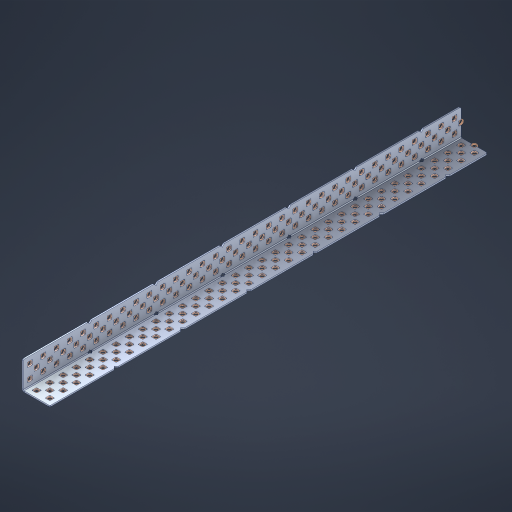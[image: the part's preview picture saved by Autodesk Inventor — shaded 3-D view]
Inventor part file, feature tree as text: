
AUTODESK INVENTOR PART (.ipt)
format: ipt  version: 2023 (Build 270158000, 158)  size: 2,227,200 bytes
history: native  units: in
note: dims shown in document units (in); Inventor stores cm internally (conversion verified against a paired STEP export)
features: other x204, extrude x196, sheet_metal_op x8, sketch x7, pattern_linear x2, mirror x1, chamfer x1
ambient origin geometry x8: Origin, YZ Plane, XZ Plane, XY Plane, X Axis, Y Axis, Z Axis, Center Point
bodies: Solid1 (feature_tree), Body (feature_tree)
feature tree (419):
  sheet_metal_op  "Flanges"
  sheet_metal_op  "Body Pattern"
  pattern_linear  "Center Pattern"  Spacing1=1.0in  [1 undecoded]
  other  "Arc Length"
  pattern_linear  "Notch Pattern"  Spacing1=0.1875in  [1 undecoded]
  other  "Diagonal Plane"
  mirror  "Everything Mirrored"
  chamfer  "End Chamfer"
  sketch  "Sketch1"  dims[d0=1.0in]
  other  "Plate1"
  sketch  "Sketch2"  dims[d1=16.5in]
  other  "Plate2"
  sheet_metal_op  "Bend1"
  sheet_metal_op  "Corner1"
  sketch  "Sketch8"  dims[d2=0.0469in]
  sketch  "Sketch9"  dims[d3=0.0469in]
  other  "Srf91"
  sheet_metal_op  "Body Pattern Sketch"
  other  "Srf92"
  sketch  "Sketch13"  dims[d4=0.0234in]
  sketch  "Sketch15"  dims[d5=0.0938in]
  sketch  "Sketch16"  dims[d6=0.0469in d7=1.0in d8=90.0deg d9=0.0312in d10=0.1875in d11=0.0469in d12=0.0469in d49=0.182in d50=0.02in d52=0.25in d53=0.0469in d54=0.0in d55=0.172in d56=1.0in d57=0.0in d60=12.9921in d62=0.5in d63=0.7874in d65=0.5in d85=0.1473in d86=0.1659in d89=0.0469in d90=0.0in d91=0.04in d92=0.0491in d95=2.5in d96=0.04in d97=0.25in d98=45.0deg d99=0.25in d106=0.182in d107=0.02in d108=0.5in d110=0.0469in d111=0.0in d112=0.172in d113=0.5in d114=0.0in d117=0.5in d123=0.25in d125=0.25in d126=0.0491in d127=0.1227in d128=0.08in d129=0.04in d130=2.5in]
  other  "Srf786"
  other  "Srf856"
  other  "Srf857"
  other  "Srf858"
  other  "Srf859"
  other  "Srf860"
  other  "Srf861"
  other  "Srf889"
  other  "Srf890"
  other  "Srf891"
  other  "Srf1275"
  other  "Srf1276"
  other  "Srf1278"
  other  "Srf1279"
  other  "Srf1280"
  other  "Srf1281"
  other  "Srf1282"
  other  "Srf1283"
  other  "Srf1277"
  other  "Srf1285"
  other  "Srf1286"
  other  "Srf1287"
  other  "Srf1383"
  other  "Srf1384"
  other  "Srf1385"
  other  "Srf1386"
  other  "Srf1387"
  other  "Srf1388"
  other  "Srf1389"
  other  "Srf1390"
  other  "Srf1391"
  other  "Srf1392"
  other  "Srf1393"
  other  "Srf1394"
  other  "Srf1395"
  other  "Srf1396"
  other  "Srf1397"
  other  "Srf1398"
  other  "Srf1399"
  other  "Srf1400"
  other  "Srf1401"
  other  "Srf1402"
  other  "Srf1403"
  other  "Srf1404"
  other  "Srf1405"
  other  "Srf1406"
  other  "Srf1407"
  other  "Srf1408"
  other  "Srf1409"
  other  "Srf1410"
  other  "Srf1411"
  other  "Srf1412"
  other  "Srf1413"
  other  "Srf1414"
  other  "Srf1415"
  other  "Srf1416"
  other  "Srf1417"
  other  "Srf1418"
  other  "Srf1419"
  other  "Srf1420"
  other  "Srf1421"
  other  "Srf1422"
  other  "Srf1423"
  other  "Srf1424"
  other  "Srf1425"
  other  "Srf1426"
  other  "Srf1427"
  other  "Srf1428"
  other  "Srf1429"
  other  "Srf1430"
  other  "Srf1431"
  other  "Srf1432"
  other  "Srf1433"
  other  "Srf1434"
  other  "Srf1435"
  other  "Srf1436"
  other  "Srf1437"
  other  "Srf1438"
  other  "Srf1439"
  other  "Srf1440"
  other  "Srf1445"
  other  "Srf1446"
  other  "Srf1447"
  other  "Srf1448"
  other  "Srf1449"
  other  "Srf1450"
  other  "Srf1451"
  other  "Srf1452"
  other  "Srf1453"
  other  "Srf1454"
  other  "Srf1455"
  other  "Srf1456"
  other  "Srf1457"
  other  "Srf1458"
  other  "Srf1459"
  other  "Srf1460"
  other  "Srf1461"
  other  "Srf1462"
  other  "Srf1463"
  other  "Srf1464"
  other  "Srf1465"
  other  "Srf1466"
  other  "Srf1467"
  other  "Srf1468"
  other  "Srf1469"
  other  "Srf1470"
  other  "Srf1471"
  other  "Srf1472"
  other  "Srf1473"
  other  "Srf1475"
  other  "Srf1476"
  other  "Srf1477"
  other  "Srf1478"
  other  "Srf1479"
  other  "Srf1480"
  other  "Srf1481"
  other  "Srf1482"
  other  "Srf1483"
  other  "Srf1484"
  other  "Srf1485"
  other  "Srf1486"
  other  "Srf1487"
  other  "Srf1488"
  other  "Srf1489"
  other  "Srf1490"
  other  "Srf1491"
  other  "Srf1492"
  other  "Srf1493"
  other  "Srf1494"
  other  "Srf1495"
  other  "Srf1496"
  other  "Srf1497"
  other  "Srf1498"
  other  "Srf1499"
  other  "Srf1500"
  other  "Srf1501"
  other  "Srf1502"
  other  "Srf1503"
  other  "Srf1504"
  other  "Srf1505"
  other  "Srf1506"
  other  "Srf1507"
  other  "Srf1508"
  other  "Srf1509"
  other  "Srf1510"
  other  "Srf1511"
  other  "Srf1512"
  other  "Srf1513"
  other  "Srf1514"
  other  "Srf1515"
  other  "Srf1516"
  other  "Srf1517"
  other  "Srf1518"
  other  "Srf1519"
  other  "Srf1520"
  other  "Srf1521"
  other  "Srf1522"
  other  "Srf1523"
  other  "Srf1524"
  other  "Srf1525"
  other  "Srf1526"
  other  "Srf1527"
  other  "Srf1528"
  other  "Srf1529"
  other  "Srf1530"
  other  "Srf1531"
  other  "Srf1532"
  other  "Srf1537"
  other  "Srf1538"
  other  "Srf1539"
  other  "Srf1540"
  other  "Srf1541"
  other  "Srf1542"
  other  "Srf1543"
  other  "Srf1544"
  other  "Srf1545"
  other  "Srf1546"
  other  "Srf1547"
  other  "Srf1548"
  other  "Srf1549"
  other  "Srf1550"
  other  "Srf1551"
  other  "Srf1552"
  other  "Srf1553"
  other  "Srf1554"
  other  "Srf1555"
  other  "Srf1556"
  other  "Srf1557"
  other  "Srf1558"
  other  "Srf1559"
  other  "Srf1560"
  other  "Srf1561"
  other  "Srf1562"
  other  "Srf1563"
  other  "Srf1564"
  other  "Srf1565"
  sheet_metal_op  "Body Stamp"
  sheet_metal_op  "Body Circle"
  other  "Center Stamp"
  other  "Center Circle"
  sheet_metal_op  "Notch"
  extrude  "ExtrusionSrf92"  Depth=0.0469in
  extrude  "ExtrusionSrf856"  Depth=0.0469in
  extrude  "ExtrusionSrf857"  Depth=0.182in
  extrude  "ExtrusionSrf858"  Depth=0.02in
  extrude  "ExtrusionSrf859"  Depth=0.25in
  extrude  "ExtrusionSrf860"  Depth=0.0469in
  extrude  "ExtrusionSrf861"  TaperAngle=0.0deg  [1 undecoded]
  extrude  "ExtrusionSrf889"  Depth=2.5in
  extrude  "ExtrusionSrf890"  Depth=1.0in TaperAngle=0.0deg
  extrude  "ExtrusionSrf891"  Depth=2.5in
  extrude  "ExtrusionSrf1275"  Depth=0.5in
  extrude  "ExtrusionSrf1276"  Depth=2.5in
  extrude  "ExtrusionSrf1277"  Depth=2.5in
  extrude  "ExtrusionSrf1278"  Depth=0.0469in
  extrude  "ExtrusionSrf1279"  Depth=2.5in TaperAngle=0.0deg
  extrude  "ExtrusionSrf1280"  Depth=2.5in
  extrude  "ExtrusionSrf1281"  Depth=0.25in TaperAngle=45.0deg
  extrude  "ExtrusionSrf1282"  Depth=0.25in
  extrude  "ExtrusionSrf1345"  Depth=0.182in
  extrude  "ExtrusionSrf1346"  Depth=0.02in
  extrude  "ExtrusionSrf1347"  Depth=0.5in
  extrude  "ExtrusionSrf1348"  Depth=0.0469in
  extrude  "ExtrusionSrf1383"  TaperAngle=0.0deg  [1 undecoded]
  extrude  "ExtrusionSrf1384"  Depth=2.5in
  extrude  "ExtrusionSrf1385"  Depth=0.5in TaperAngle=0.0deg
  extrude  "ExtrusionSrf1386"  Depth=0.5in
  extrude  "ExtrusionSrf1387"  Depth=0.25in
  extrude  "ExtrusionSrf1388"  Depth=0.25in
  extrude  "ExtrusionSrf1389"  Depth=2.5in
  extrude  "ExtrusionSrf1390"  Depth=2.5in
  extrude  "ExtrusionSrf1391"  Depth=2.5in
  extrude  "ExtrusionSrf1392"  Depth=2.5in
  extrude  "ExtrusionSrf1393"  Depth=2.5in
  extrude  "ExtrusionSrf1394"  [1 undecoded]
  extrude  "ExtrusionSrf1395"  [1 undecoded]
  extrude  "ExtrusionSrf1396"  [1 undecoded]
  extrude  "ExtrusionSrf1397"  [1 undecoded]
  extrude  "ExtrusionSrf1398"  [1 undecoded]
  extrude  "ExtrusionSrf1399"  [1 undecoded]
  extrude  "ExtrusionSrf1400"  [1 undecoded]
  extrude  "ExtrusionSrf1401"  [1 undecoded]
  extrude  "ExtrusionSrf1402"  [1 undecoded]
  extrude  "ExtrusionSrf1403"  [1 undecoded]
  extrude  "ExtrusionSrf1404"  [1 undecoded]
  extrude  "ExtrusionSrf1405"  [1 undecoded]
  extrude  "ExtrusionSrf1406"  [1 undecoded]
  extrude  "ExtrusionSrf1407"  [1 undecoded]
  extrude  "ExtrusionSrf1408"  [1 undecoded]
  extrude  "ExtrusionSrf1409"  [1 undecoded]
  extrude  "ExtrusionSrf1410"  [1 undecoded]
  extrude  "ExtrusionSrf1411"  [1 undecoded]
  extrude  "ExtrusionSrf1412"  [1 undecoded]
  extrude  "ExtrusionSrf1413"  [1 undecoded]
  extrude  "ExtrusionSrf1414"  [1 undecoded]
  extrude  "ExtrusionSrf1415"  [1 undecoded]
  extrude  "ExtrusionSrf1416"  [1 undecoded]
  extrude  "ExtrusionSrf1417"  [1 undecoded]
  extrude  "ExtrusionSrf1418"  [1 undecoded]
  extrude  "ExtrusionSrf1419"  [1 undecoded]
  extrude  "ExtrusionSrf1420"  [1 undecoded]
  extrude  "ExtrusionSrf1421"  [1 undecoded]
  extrude  "ExtrusionSrf1422"  [1 undecoded]
  extrude  "ExtrusionSrf1423"  [1 undecoded]
  extrude  "ExtrusionSrf1424"  [1 undecoded]
  extrude  "ExtrusionSrf1425"  [1 undecoded]
  extrude  "ExtrusionSrf1426"  [1 undecoded]
  extrude  "ExtrusionSrf1427"  [1 undecoded]
  extrude  "ExtrusionSrf1428"  [1 undecoded]
  extrude  "ExtrusionSrf1429"  [1 undecoded]
  extrude  "ExtrusionSrf1430"  [1 undecoded]
  extrude  "ExtrusionSrf1431"  [1 undecoded]
  extrude  "ExtrusionSrf1432"  [1 undecoded]
  extrude  "ExtrusionSrf1433"  [1 undecoded]
  extrude  "ExtrusionSrf1434"  [1 undecoded]
  extrude  "ExtrusionSrf1435"  [1 undecoded]
  extrude  "ExtrusionSrf1436"  [1 undecoded]
  extrude  "ExtrusionSrf1437"  [1 undecoded]
  extrude  "ExtrusionSrf1438"  [1 undecoded]
  extrude  "ExtrusionSrf1439"  [1 undecoded]
  extrude  "ExtrusionSrf1440"  [1 undecoded]
  extrude  "ExtrusionSrf1445"  [1 undecoded]
  extrude  "ExtrusionSrf1446"  [1 undecoded]
  extrude  "ExtrusionSrf1447"  [1 undecoded]
  extrude  "ExtrusionSrf1448"  [1 undecoded]
  extrude  "ExtrusionSrf1449"  [1 undecoded]
  extrude  "ExtrusionSrf1450"  [1 undecoded]
  extrude  "ExtrusionSrf1451"  [1 undecoded]
  extrude  "ExtrusionSrf1452"  [1 undecoded]
  extrude  "ExtrusionSrf1453"  [1 undecoded]
  extrude  "ExtrusionSrf1454"  [1 undecoded]
  extrude  "ExtrusionSrf1455"  [1 undecoded]
  extrude  "ExtrusionSrf1456"  [1 undecoded]
  extrude  "ExtrusionSrf1457"  [1 undecoded]
  extrude  "ExtrusionSrf1458"  [1 undecoded]
  extrude  "ExtrusionSrf1459"  [1 undecoded]
  extrude  "ExtrusionSrf1460"  [1 undecoded]
  extrude  "ExtrusionSrf1461"  [1 undecoded]
  extrude  "ExtrusionSrf1462"  [1 undecoded]
  extrude  "ExtrusionSrf1463"  [1 undecoded]
  extrude  "ExtrusionSrf1464"  [1 undecoded]
  extrude  "ExtrusionSrf1465"  [1 undecoded]
  extrude  "ExtrusionSrf1466"  [1 undecoded]
  extrude  "ExtrusionSrf1467"  [1 undecoded]
  extrude  "ExtrusionSrf1468"  [1 undecoded]
  extrude  "ExtrusionSrf1469"  [1 undecoded]
  extrude  "ExtrusionSrf1470"  [1 undecoded]
  extrude  "ExtrusionSrf1471"  [1 undecoded]
  extrude  "ExtrusionSrf1472"  [1 undecoded]
  extrude  "ExtrusionSrf1473"  [1 undecoded]
  extrude  "ExtrusionSrf1475"  [1 undecoded]
  extrude  "ExtrusionSrf1476"  [1 undecoded]
  extrude  "ExtrusionSrf1477"  [1 undecoded]
  extrude  "ExtrusionSrf1478"  [1 undecoded]
  extrude  "ExtrusionSrf1479"  [1 undecoded]
  extrude  "ExtrusionSrf1480"  [1 undecoded]
  extrude  "ExtrusionSrf1481"  [1 undecoded]
  extrude  "ExtrusionSrf1482"  [1 undecoded]
  extrude  "ExtrusionSrf1483"  [1 undecoded]
  extrude  "ExtrusionSrf1484"  [1 undecoded]
  extrude  "ExtrusionSrf1485"  [1 undecoded]
  extrude  "ExtrusionSrf1486"  [1 undecoded]
  extrude  "ExtrusionSrf1487"  [1 undecoded]
  extrude  "ExtrusionSrf1488"  [1 undecoded]
  extrude  "ExtrusionSrf1489"  [1 undecoded]
  extrude  "ExtrusionSrf1490"  [1 undecoded]
  extrude  "ExtrusionSrf1491"  [1 undecoded]
  extrude  "ExtrusionSrf1492"  [1 undecoded]
  extrude  "ExtrusionSrf1493"  [1 undecoded]
  extrude  "ExtrusionSrf1494"  [1 undecoded]
  extrude  "ExtrusionSrf1495"  [1 undecoded]
  extrude  "ExtrusionSrf1496"  [1 undecoded]
  extrude  "ExtrusionSrf1497"  [1 undecoded]
  extrude  "ExtrusionSrf1498"  [1 undecoded]
  extrude  "ExtrusionSrf1499"  [1 undecoded]
  extrude  "ExtrusionSrf1500"  [1 undecoded]
  extrude  "ExtrusionSrf1501"  [1 undecoded]
  extrude  "ExtrusionSrf1502"  [1 undecoded]
  extrude  "ExtrusionSrf1503"  [1 undecoded]
  extrude  "ExtrusionSrf1504"  [1 undecoded]
  extrude  "ExtrusionSrf1505"  [1 undecoded]
  extrude  "ExtrusionSrf1506"  [1 undecoded]
  extrude  "ExtrusionSrf1507"  [1 undecoded]
  extrude  "ExtrusionSrf1508"  [1 undecoded]
  extrude  "ExtrusionSrf1509"  [1 undecoded]
  extrude  "ExtrusionSrf1510"  [1 undecoded]
  extrude  "ExtrusionSrf1511"  [1 undecoded]
  extrude  "ExtrusionSrf1512"  [1 undecoded]
  extrude  "ExtrusionSrf1513"  [1 undecoded]
  extrude  "ExtrusionSrf1514"  [1 undecoded]
  extrude  "ExtrusionSrf1515"  [1 undecoded]
  extrude  "ExtrusionSrf1516"  [1 undecoded]
  extrude  "ExtrusionSrf1517"  [1 undecoded]
  extrude  "ExtrusionSrf1518"  [1 undecoded]
  extrude  "ExtrusionSrf1519"  [1 undecoded]
  extrude  "ExtrusionSrf1520"  [1 undecoded]
  extrude  "ExtrusionSrf1521"  [1 undecoded]
  extrude  "ExtrusionSrf1522"  [1 undecoded]
  extrude  "ExtrusionSrf1523"  [1 undecoded]
  extrude  "ExtrusionSrf1524"  [1 undecoded]
  extrude  "ExtrusionSrf1525"  [1 undecoded]
  extrude  "ExtrusionSrf1526"  [1 undecoded]
  extrude  "ExtrusionSrf1527"  [1 undecoded]
  extrude  "ExtrusionSrf1528"  [1 undecoded]
  extrude  "ExtrusionSrf1529"  [1 undecoded]
  extrude  "ExtrusionSrf1530"  [1 undecoded]
  extrude  "ExtrusionSrf1531"  [1 undecoded]
  extrude  "ExtrusionSrf1532"  [1 undecoded]
  extrude  "ExtrusionSrf1537"  [1 undecoded]
  extrude  "ExtrusionSrf1538"  [1 undecoded]
  extrude  "ExtrusionSrf1539"  [1 undecoded]
  extrude  "ExtrusionSrf1540"  [1 undecoded]
  extrude  "ExtrusionSrf1541"  [1 undecoded]
  extrude  "ExtrusionSrf1542"  [1 undecoded]
  extrude  "ExtrusionSrf1543"  [1 undecoded]
  extrude  "ExtrusionSrf1544"  [1 undecoded]
  extrude  "ExtrusionSrf1545"  [1 undecoded]
  extrude  "ExtrusionSrf1546"  [1 undecoded]
  extrude  "ExtrusionSrf1547"  [1 undecoded]
  extrude  "ExtrusionSrf1548"  [1 undecoded]
  extrude  "ExtrusionSrf1549"  [1 undecoded]
  extrude  "ExtrusionSrf1550"  [1 undecoded]
  extrude  "ExtrusionSrf1551"  [1 undecoded]
  extrude  "ExtrusionSrf1552"  [1 undecoded]
  extrude  "ExtrusionSrf1553"  [1 undecoded]
  extrude  "ExtrusionSrf1554"  [1 undecoded]
  extrude  "ExtrusionSrf1555"  [1 undecoded]
  extrude  "ExtrusionSrf1556"  [1 undecoded]
  extrude  "ExtrusionSrf1557"  [1 undecoded]
  extrude  "ExtrusionSrf1558"  [1 undecoded]
  extrude  "ExtrusionSrf1559"  [1 undecoded]
  extrude  "ExtrusionSrf1560"  [1 undecoded]
  extrude  "ExtrusionSrf1561"  [1 undecoded]
  extrude  "ExtrusionSrf1562"  [1 undecoded]
  extrude  "ExtrusionSrf1563"  [1 undecoded]
  extrude  "ExtrusionSrf1564"  [1 undecoded]
  extrude  "ExtrusionSrf1565"  [1 undecoded]
note: 167 required parameter values undecoded (feature->parameter linkage not recoverable at this tier; creation-order binding heuristic only, values carry confidence <= 0.55)
